# Revit family: Zumtobel PANOS3 R R200
name_source: partatom
category: Lighting Fixtures
revit_build: Autodesk Revit 2018 (Build: 20170223_1515(x64)
units: mm (PartAtom-declared; Revit-internal decimal feet)

## family parameters
Cut with Voids When Loaded = No
Host = Face
Light Source = Yes
OmniClass Number = 23.80.70.11
OmniClass Title = Luminaries for Internal Lighting
Part Type = Normal
Room Calculation Point = No
Round Connector Dimension = Use Diameter
Shared = No

## types (4) — shared parameters
Apparent Load = 8 VA
Assembly Code = D5020200
Body = ZG_Metal_White
Color Filter = 16777215
Cover Diameter = 218 mm
Cutout Diameter = 200 mm
Description = LED ceiling-recessed luminaire
Dimming Lamp Color Temperature Shift = <None>
Emit Shape Visible in Rendering = Yes
Emit from Circle Diameter = 218 mm
Lamp = LED
Manufacturer = Zumtobel Lighting
Reflector = ZG_Metal_White_Self_Illumination
Tilt Angle = -90.00°
URL = http://www.zumtobel.com
Voltage = 230 V
zero-valued in all types: Default Elevation

## per-type parameters (varying)
| type | Clearance Height | Height | Length | Model | Photometric Web File | R200H | R200L | WH | Width |
| PANOS3 R R200L WH | 75 mm | 65 mm | 213 mm | 60819287 | 60819287_(STD).IES | No | Yes | Yes | 213 mm |
| PANOS3 R R200L TL | 75 mm | 65 mm | 200 mm | 60819285 | 60819285_(STD).IES | No | Yes | No | 200 mm |
| PANOS3 R R200H WH | 120 mm  [stored 0.393701 ft] | 106 mm  [stored 0.347769 ft] | 213 mm | 60819247 | 60819247_(STD).IES | Yes | No | Yes | 213 mm |
| PANOS3 R R200H TL | 120 mm  [stored 0.393701 ft] | 106 mm  [stored 0.347769 ft] | 200 mm | 60818282 | 60819282_(STD).IES | Yes | No | No | 200 mm |

note: [stored X ft] marks values corroborated as IEEE doubles in the binary element streams (Revit-internal decimal feet)

## geometry (parser evidence)
native form markers: Sweep x3
no freeform markers — native parametric forms only
